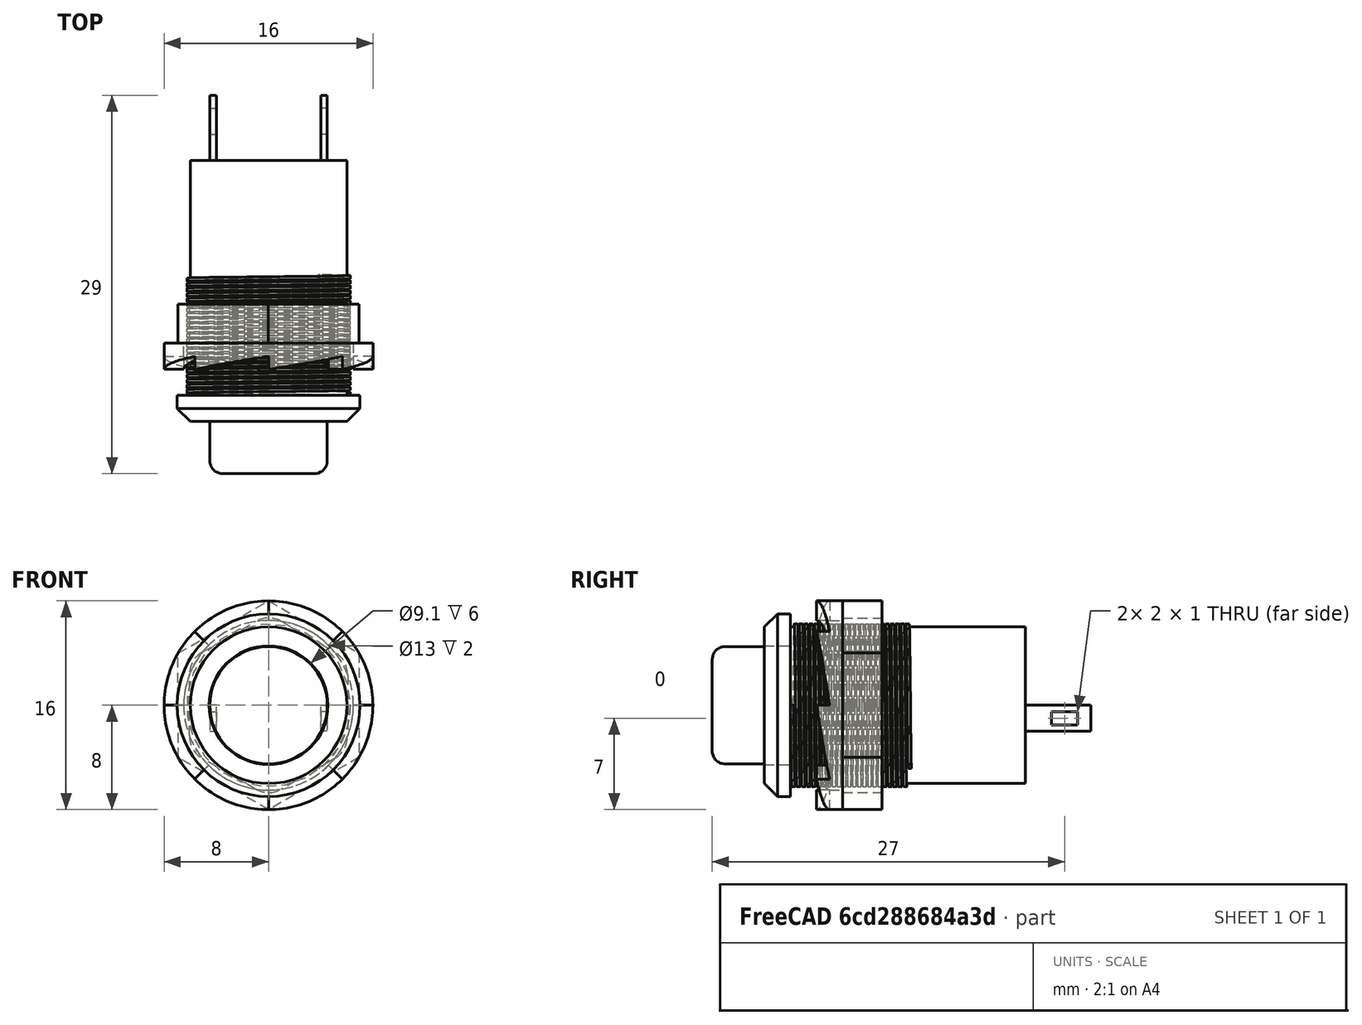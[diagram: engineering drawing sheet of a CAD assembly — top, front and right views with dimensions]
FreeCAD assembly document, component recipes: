
FREECAD ASSEMBLY — COMPONENT RECIPES ("spring_button")

This assembly document has 4 components, labeled P0..P3 below (a component is one placed body or linked part). 4 of them carry a construction recipe — the FreeCAD feature program that regenerates the part from scratch, quoted from this document or its linked companion documents; the rest are supplied as boundary geometry only. No exploded tour is included for this assembly.
COMPONENT P0 — recipe-attached ("base001", modeled in this document).
Construction recipe (the document's own serialized feature program — sketch geometry with constraints, then the solid features built on it; lengths are millimeters unless a unit is written):

FEATURE [Sketcher::SketchObject] Sketch
  ArcFitTolerance = 1e-06
  AttachmentSupport = -> [Origin]
  ExternalTypes = [0]
  FullyConstrained = true
  MakeInternals = false
  MapMode = 5
  Placement = pos=(0,0,0) rot=(1,0,0;1.5708rad)
  _ExternalGeoVersion = 1
  sketch-geometry (1):
    g0: Circle CenterX=0 CenterY=0 CenterZ=0 NormalX=0 NormalY=0 NormalZ=1 AngleXU=0 Radius=6
  constraints (2):
    c: Diameter(g0) = 12
    c: Coincident(g0,g-1)
FEATURE [PartDesign::Pad] Pad
  Direction = (0,-1,2e-16)
  Length = 18
  Length2 = 10
  Profile = -> Sketch
  ReferenceAxis = -> Sketch [N_Axis]
  Refine = true
  SideType = 0
  Suppressed = false
  Type = 0
  Type2 = 0
FEATURE [Sketcher::SketchObject] Sketch001
  ArcFitTolerance = 1e-06
  AttachmentSupport = -> [Pad]
  ExternalTypes = [0]
  FullyConstrained = true
  MakeInternals = false
  MapMode = 5
  Placement = pos=(0,-18,0) rot=(1,0,0;1.5708rad)
  _ExternalGeoVersion = 1
  sketch-geometry (1):
    g0: Circle CenterX=0 CenterY=0 CenterZ=0 NormalX=0 NormalY=0 NormalZ=1 AngleXU=0 Radius=7
  constraints (2):
    c: Diameter(g0) = 14
    c: Coincident(g0,g-1)
FEATURE [PartDesign::Pad] Pad001
  BaseFeature = -> Pad
  Direction = (0,-1,2e-16)
  Length = 2
  Length2 = 10
  Profile = -> Sketch001
  ReferenceAxis = -> Sketch001 [N_Axis]
  Refine = true
  SideType = 0
  Suppressed = false
  Type = 0
  Type2 = 0
FEATURE [PartDesign::Chamfer] Chamfer
  Angle = 45
  Base = -> Pad001 [Edge6]
  BaseFeature = -> Pad001
  ChamferType = 0
  FlipDirection = false
  Refine = true
  Size = 1
  Size2 = 1
  SupportTransform = false
  Suppressed = false
  UseAllEdges = false
FEATURE [PartDesign::Hole] Hole
  BaseFeature = -> Chamfer
  BaseProfileType = 7
  CustomThreadClearance = 0
  Depth = 6
  DepthType = 0
  Diameter = 9.1
  DrillForDepth = false
  DrillPoint = 0
  DrillPointAngle = 118
  HoleCutCountersinkAngle = 90
  HoleCutCustomValues = false
  HoleCutDepth = 0
  HoleCutDiameter = 0
  HoleCutType = 0
  ModelThread = false
  Profile = -> Chamfer [Face4]
  Refine = true
  Suppressed = false
  Tapered = false
  TaperedAngle = 90
  ThreadClass = 0
  ThreadDepth = 6
  ThreadDepthType = 0
  ThreadDiameter = 9.1
  ThreadDirection = 0
  ThreadFit = 0
  ThreadSize = 0
  ThreadType = 0
  Threaded = false
  UseCustomThreadClearance = false
FEATURE [Sketcher::SketchObject] Sketch004
  ArcFitTolerance = 1e-06
  AttachmentSupport = -> [Origin]
  ExternalTypes = [0]
  FullyConstrained = true
  MakeInternals = false
  MapMode = 5
  _ExternalGeoVersion = 1
  sketch-geometry (4):
    g0: LineSegment StartX=6 StartY=-18 StartZ=0 EndX=6.25 EndY=-18 EndZ=0
    g1: LineSegment StartX=6.25 StartY=-18 StartZ=0 EndX=6.25 EndY=-17.75 EndZ=0
    g2: LineSegment StartX=6.25 StartY=-17.75 StartZ=0 EndX=6 EndY=-17.75 EndZ=0
    g3: LineSegment StartX=6 StartY=-17.75 StartZ=0 EndX=6 EndY=-18 EndZ=0
  constraints (11):
    c: Coincident(g0,g-3)
    c: Horizontal(g0)
    c: Coincident(g1,g0)
    c: Vertical(g1)
    c: Coincident(g2,g1)
    c: PointOnObject(g2,g-3)
    c: Horizontal(g2)
    c: DistanceY(g1,g1) = 0.25
    c: DistanceX(g2,g2) = 0.25
    c: Coincident(g3,g2)
    c: Coincident(g3,g0)
FEATURE [PartDesign::AdditiveHelix] AdditiveHelix
  Angle = 0
  Axis = (0,1,0)
  Base = (0,0,0)
  BaseFeature = -> Hole
  Growth = 0
  HasBeenEdited = true
  Height = 9
  LeftHanded = false
  Mode = 0
  Outside = false
  Pitch = 0.388909
  Profile = -> Sketch004
  ReferenceAxis = -> Sketch004 [V_Axis]
  Refine = true
  Suppressed = false
  Tolerance = 0.1
  Turns = 23.1417
FEATURE [PartDesign::Body] Body  label="base"
  AllowCompound = true
  Group = -> [Sketch,Pad,Sketch001,Pad001,Chamfer,Hole,Sketch004,AdditiveHelix]
  Origin = -> Origin
  Tip = -> AdditiveHelix
COMPONENT P1 — recipe-attached ("button001", modeled in this document).
Construction recipe (the document's own serialized feature program — sketch geometry with constraints, then the solid features built on it; lengths are millimeters unless a unit is written):

FEATURE [PartDesign::ShapeBinder] CopyAdditiveHelix001
  Placement = pos=(0,-20,0) rot=(0,0,1;0rad)
  TraceSupport = false
FEATURE [PartDesign::Plane] DatumPlane001
  AttachmentSupport = -> [CopyAdditiveHelix001]
  Length = 60
  MapMode = 11
  Placement = pos=(0,-20,0) rot=(0.57735,0.57735,-0.57735;2.0944rad)
  ResizeMode = 0
  Width = 60
FEATURE [Sketcher::SketchObject] Sketch007
  ArcFitTolerance = 1e-06
  AttachmentSupport = -> [DatumPlane001]
  ExternalTypes = [0]
  FullyConstrained = true
  MakeInternals = false
  MapMode = 5
  Placement = pos=(0,-20,0) rot=(0.57735,0.57735,-0.57735;2.0944rad)
  _ExternalGeoVersion = 1
  sketch-geometry (1):
    g0: Circle CenterX=0 CenterY=0 CenterZ=0 NormalX=0 NormalY=0 NormalZ=1 AngleXU=0 Radius=4.5
  constraints (2):
    c: Diameter(g0) = 9
    c: Coincident(g0,g-1)
FEATURE [PartDesign::Pad] Pad003
  Direction = (0,-1,0)
  Length = 4
  Length2 = 10
  Placement = pos=(0,-20,0) rot=(0.57735,0.57735,-0.57735;2.0944rad)
  Profile = -> Sketch007
  ReferenceAxis = -> Sketch007 [N_Axis]
  Refine = true
  SideType = 0
  Suppressed = false
  Type = 0
  Type2 = 0
FEATURE [PartDesign::Fillet] Fillet
  Base = -> Pad003 [Edge3]
  BaseFeature = -> Pad003
  Placement = pos=(0,-20,0) rot=(0.57735,0.57735,-0.57735;2.0944rad)
  Radius = 1
  Refine = true
  SupportTransform = false
  Suppressed = false
  UseAllEdges = false
FEATURE [PartDesign::Body] Body002  label="button"
  AllowCompound = true
  Group = -> [DatumPlane001,CopyAdditiveHelix001,Sketch007,Pad003,Fillet]
  Origin = -> Origin004
  Tip = -> Fillet
COMPONENT P2 — recipe-attached ("nut001", modeled in this document).
Construction recipe (the document's own serialized feature program — sketch geometry with constraints, then the solid features built on it; lengths are millimeters unless a unit is written):

FEATURE [Sketcher::SketchObject] Sketch008
  ArcFitTolerance = 1e-06
  AttachmentSupport = -> [Origin006]
  ExternalTypes = [0]
  FullyConstrained = true
  MakeInternals = false
  MapMode = 5
  Placement = pos=(0,0,0) rot=(1,0,0;1.5708rad)
  _ExternalGeoVersion = 1
  sketch-geometry (2):
    g0: Circle CenterX=0 CenterY=0 CenterZ=0 NormalX=0 NormalY=0 NormalZ=1 AngleXU=0 Radius=8
    g1: Circle CenterX=0 CenterY=0 CenterZ=0 NormalX=0 NormalY=0 NormalZ=1 AngleXU=0 Radius=6.5
  constraints (4):
    c: Diameter(g0) = 16
    c: Coincident(g0,g-1)
    c: Diameter(g1) = 13
    c: Coincident(g1,g0)
FEATURE [PartDesign::Pad] Pad004
  Direction = (0,-1,2e-16)
  Length = 2
  Length2 = 10
  Profile = -> Sketch008
  ReferenceAxis = -> Sketch008 [N_Axis]
  Refine = true
  SideType = 0
  Suppressed = false
  Type = 0
  Type2 = 0
FEATURE [Sketcher::SketchObject] Sketch009
  ArcFitTolerance = 1e-06
  AttachmentSupport = -> [Origin006]
  ExternalGeometry = -> [Pad004]
  ExternalTypes = [0,0]
  FullyConstrained = true
  MakeInternals = false
  MapMode = 5
  _ExternalGeoVersion = 1
  sketch-geometry (4):
    g0: LineSegment StartX=6.5 StartY=-2 StartZ=0 EndX=8 EndY=-2 EndZ=0
    g1: LineSegment StartX=8 StartY=-2 StartZ=0 EndX=8 EndY=-1 EndZ=0
    g2: LineSegment StartX=8 StartY=-1 StartZ=0 EndX=6.5 EndY=-1 EndZ=0
    g3: LineSegment StartX=6.5 StartY=-1 StartZ=0 EndX=6.5 EndY=-2 EndZ=0
  constraints (11):
    c: Coincident(g0,g1)
    c: Coincident(g1,g2)
    c: Coincident(g2,g3)
    c: Coincident(g3,g0)
    c: Horizontal(g0)
    c: Horizontal(g2)
    c: Vertical(g1)
    c: Vertical(g3)
    c: Coincident(g0,g-4)
    c: PointOnObject(g1,g-3)
    c: DistanceY(g1,g1) = 1
FEATURE [PartDesign::SubtractiveHelix] SubtractiveHelix
  Angle = 0
  Axis = (0,1,0)
  Base = (0,0,0)
  BaseFeature = -> Pad004
  Growth = 0
  HasBeenEdited = true
  Height = 1
  LeftHanded = false
  Mode = 0
  Outside = false
  Pitch = 8
  Profile = -> Sketch009
  ReferenceAxis = -> Sketch009 [V_Axis]
  Refine = true
  Reversed = true
  Suppressed = false
  Tolerance = 0.1
  Turns = 0.125
FEATURE [PartDesign::PolarPattern] PolarPattern
  Angle = 360
  Axis = -> Y_Axis003
  BaseFeature = -> SubtractiveHelix
  Mode = 0
  Occurrences = 8
  Offset = 120
  Originals = -> [SubtractiveHelix]
  Refine = true
  SpacingPattern = [0]
  Spacings = [-1,-1,-1,-1,-1,-1,-1]
  Suppressed = false
  TransformMode = 0
FEATURE [Sketcher::SketchObject] Sketch010
  ArcFitTolerance = 1e-06
  AttachmentSupport = -> [PolarPattern]
  ExternalGeometry = -> [PolarPattern]
  ExternalTypes = [0]
  FullyConstrained = false
  MakeInternals = false
  MapMode = 5
  Placement = pos=(0,0,0) rot=(0,0.707107,0.707107;3.14159rad)
  _ExternalGeoVersion = 1
  sketch-geometry (14):
    g0: LineSegment StartX=0.0147037 StartY=7.99999 StartZ=0 EndX=-6.92084 EndY=4.01273 EndZ=0
    g1: LineSegment StartX=-6.92084 StartY=4.01273 StartZ=0 EndX=-6.93554 EndY=-3.98726 EndZ=0
    g2: LineSegment StartX=-6.93554 StartY=-3.98726 StartZ=0 EndX=-0.0147037 EndY=-7.99999 EndZ=0
    g3: LineSegment StartX=-0.0147037 StartY=-7.99999 StartZ=0 EndX=6.92084 EndY=-4.01273 EndZ=0
    g4: LineSegment StartX=6.92084 StartY=-4.01273 StartZ=0 EndX=6.93554 EndY=3.98726 EndZ=0
    g5: LineSegment StartX=6.93554 StartY=3.98726 StartZ=0 EndX=0.0147037 EndY=7.99999 EndZ=0
    g6: Circle [constr] CenterX=0 CenterY=0 CenterZ=0 NormalX=0 NormalY=0 NormalZ=1 AngleXU=0 Radius=8
    g7: LineSegment StartX=0 StartY=6.99999 StartZ=0 EndX=-6.06217 EndY=3.49999 EndZ=0
    g8: LineSegment StartX=-6.06217 StartY=3.49999 StartZ=0 EndX=-6.06217 EndY=-3.49999 EndZ=0
    g9: LineSegment StartX=-6.06217 StartY=-3.49999 StartZ=0 EndX=9e-16 EndY=-6.99999 EndZ=0
    g10: LineSegment StartX=9e-16 StartY=-6.99999 StartZ=0 EndX=6.06217 EndY=-3.49999 EndZ=0
    g11: LineSegment StartX=6.06217 StartY=-3.49999 StartZ=0 EndX=6.06217 EndY=3.49999 EndZ=0
    g12: LineSegment StartX=6.06217 StartY=3.49999 StartZ=0 EndX=0 EndY=6.99999 EndZ=0
    g13: Circle [constr] CenterX=0 CenterY=0 CenterZ=0 NormalX=0 NormalY=0 NormalZ=1 AngleXU=0 Radius=6.99999
  constraints (31):
    c: Coincident(g0,g1)
    c: Coincident(g1,g2)
    c: Coincident(g2,g3)
    c: Coincident(g3,g4)
    c: Coincident(g4,g5)
    c: Coincident(g5,g0)
    c: Equal(g0, g1-g5) x5
    c: PointOnObject(g0,g6)
    c: PointOnObject(g1,g6)
    c: PointOnObject(g2,g6)
    c: PointOnObject(g3,g6)
    c: PointOnObject(g4,g6)
    c: PointOnObject(g5,g6)
    c: Coincident(g6,g-3)
    c: PointOnObject(g5,g-3)
    c: Coincident(g7,g8)
    c: Coincident(g8,g9)
    c: Coincident(g9,g10)
    c: Coincident(g10,g11)
    c: Coincident(g11,g12)
    c: Coincident(g12,g7)
    c: Equal(g7, g8-g12) x5
    c: PointOnObject(g7,g13)
    c: PointOnObject(g8,g13)
    c: PointOnObject(g9,g13)
    c: PointOnObject(g10,g13)
    c: PointOnObject(g11,g13)
    c: PointOnObject(g12,g13)
    c: Coincident(g13,g6)
    c: PointOnObject(g12,g-2)
    c: DistanceY(g7,g0) = 1
FEATURE [PartDesign::Pad] Pad005
  BaseFeature = -> PolarPattern
  Direction = (0,1,-2e-16)
  Length = 3
  Length2 = 10
  Profile = -> Sketch010
  ReferenceAxis = -> Sketch010 [N_Axis]
  Refine = true
  SideType = 0
  Suppressed = false
  Type = 0
  Type2 = 0
FEATURE [PartDesign::Fillet] Fillet001
  Base = -> Pad005 [Edge113,Edge118,Edge117,Edge114,Edge116,Edge115]
  BaseFeature = -> Pad005
  Radius = 2
  Refine = true
  SupportTransform = false
  Suppressed = false
  UseAllEdges = false
FEATURE [PartDesign::Body] Body003  label="nut"
  AllowCompound = true
  Group = -> [Sketch008,Pad004,Sketch009,SubtractiveHelix,PolarPattern,Sketch010,Pad005,Fillet001]
  Origin = -> Origin006
  Placement = pos=(0,-14,0) rot=(0,0,1;0rad)
  Tip = -> Fillet001
COMPONENT P3 — recipe-attached ("pins001", modeled in this document).
Construction recipe (the document's own serialized feature program — sketch geometry with constraints, then the solid features built on it; lengths are millimeters unless a unit is written):

FEATURE [PartDesign::ShapeBinder] CopyAdditiveHelix
  TraceSupport = false
FEATURE [PartDesign::Plane] DatumPlane
  AttachmentSupport = -> [CopyAdditiveHelix]
  Length = 60
  MapMode = 5
  Placement = pos=(0,0,0) rot=(0,0.707107,0.707107;3.14159rad)
  ResizeMode = 0
  Width = 60
FEATURE [Sketcher::SketchObject] Sketch005
  ArcFitTolerance = 1e-06
  AttachmentSupport = -> [DatumPlane]
  ExternalGeometry = -> [CopyAdditiveHelix]
  ExternalTypes = [0]
  FullyConstrained = true
  MakeInternals = false
  MapMode = 5
  Placement = pos=(0,0,0) rot=(0,0.707107,0.707107;3.14159rad)
  _ExternalGeoVersion = 1
  sketch-geometry (4):
    g0: LineSegment StartX=4 StartY=0 StartZ=0 EndX=4.5 EndY=0 EndZ=0
    g1: LineSegment StartX=4.5 StartY=0 StartZ=0 EndX=4.5 EndY=-2 EndZ=0
    g2: LineSegment StartX=4.5 StartY=-2 StartZ=0 EndX=4 EndY=-2 EndZ=0
    g3: LineSegment StartX=4 StartY=-2 StartZ=0 EndX=4 EndY=0 EndZ=0
  constraints (12):
    c: Coincident(g0,g1)
    c: Coincident(g1,g2)
    c: Coincident(g2,g3)
    c: Coincident(g3,g0)
    c: Horizontal(g0)
    c: Horizontal(g2)
    c: Vertical(g1)
    c: Vertical(g3)
    c: Distance(g1,g3) = 0.5
    c: Distance(g0,g2) = 2
    c: PointOnObject(g0,g-1)
    c: Distance(g-3,g3) = 2
FEATURE [PartDesign::Pad] Pad002
  Direction = (0,1,-2e-16)
  Length = 5
  Length2 = 10
  Placement = pos=(0,0,0) rot=(0,0.707107,0.707107;3.14159rad)
  Profile = -> Sketch005
  ReferenceAxis = -> Sketch005 [N_Axis]
  Refine = true
  SideType = 0
  Suppressed = false
  Type = 0
  Type2 = 0
FEATURE [Sketcher::SketchObject] Sketch006
  ArcFitTolerance = 1e-06
  AttachmentSupport = -> [Pad002]
  ExternalTypes = [0]
  FullyConstrained = true
  MakeInternals = false
  MapMode = 5
  Placement = pos=(-4.5,-4e-16,4e-16) rot=(0,-1,0;1.5708rad)
  _ExternalGeoVersion = 1
  sketch-geometry (4):
    g0: LineSegment StartX=-1.5 StartY=4 StartZ=0 EndX=-1.5 EndY=2 EndZ=0
    g1: LineSegment StartX=-1.5 StartY=2 StartZ=0 EndX=-0.5 EndY=2 EndZ=0
    g2: LineSegment StartX=-0.5 StartY=2 StartZ=0 EndX=-0.5 EndY=4 EndZ=0
    g3: LineSegment StartX=-0.5 StartY=4 StartZ=0 EndX=-1.5 EndY=4 EndZ=0
  constraints (12):
    c: Coincident(g0,g1)
    c: Coincident(g1,g2)
    c: Coincident(g2,g3)
    c: Coincident(g3,g0)
    c: Vertical(g0)
    c: Vertical(g2)
    c: Horizontal(g1)
    c: Horizontal(g3)
    c: DistanceY(g2,g2) = 2
    c: DistanceX(g3,g3) = 1
    c: Distance(g-2,g2) = 0.5
    c: Distance(g-1,g1) = 2
FEATURE [PartDesign::Pocket] Pocket
  BaseFeature = -> Pad002
  Direction = (1,0,-2e-16)
  Length = 5
  Length2 = 5
  Placement = pos=(0,0,0) rot=(0,0.707107,0.707107;3.14159rad)
  Profile = -> Sketch006
  ReferenceAxis = -> Sketch006 [N_Axis]
  Refine = true
  SideType = 0
  Suppressed = false
  Type = 1
  Type2 = 0
FEATURE [PartDesign::Mirrored] Mirrored
  BaseFeature = -> Pocket
  MirrorPlane = -> YZ_Plane001
  Originals = -> [Pad002,Pocket]
  Placement = pos=(0,0,0) rot=(0,0.707107,0.707107;3.14159rad)
  Refine = true
  Suppressed = false
  TransformMode = 0
FEATURE [PartDesign::Body] Body001  label="pins"
  AllowCompound = true
  Group = -> [DatumPlane,CopyAdditiveHelix,Sketch005,Pad002,Sketch006,Pocket,Mirrored]
  Origin = -> Origin002
  Tip = -> Mirrored
PROVENANCE & LICENSES
A FreeCAD (.FCStd) document from a public repository crawl; recipes are the document's own serialized feature recipes (and, for linked parts, companion documents' recipes).
License: as declared in the source repository (recorded in the dataset sidecar).
